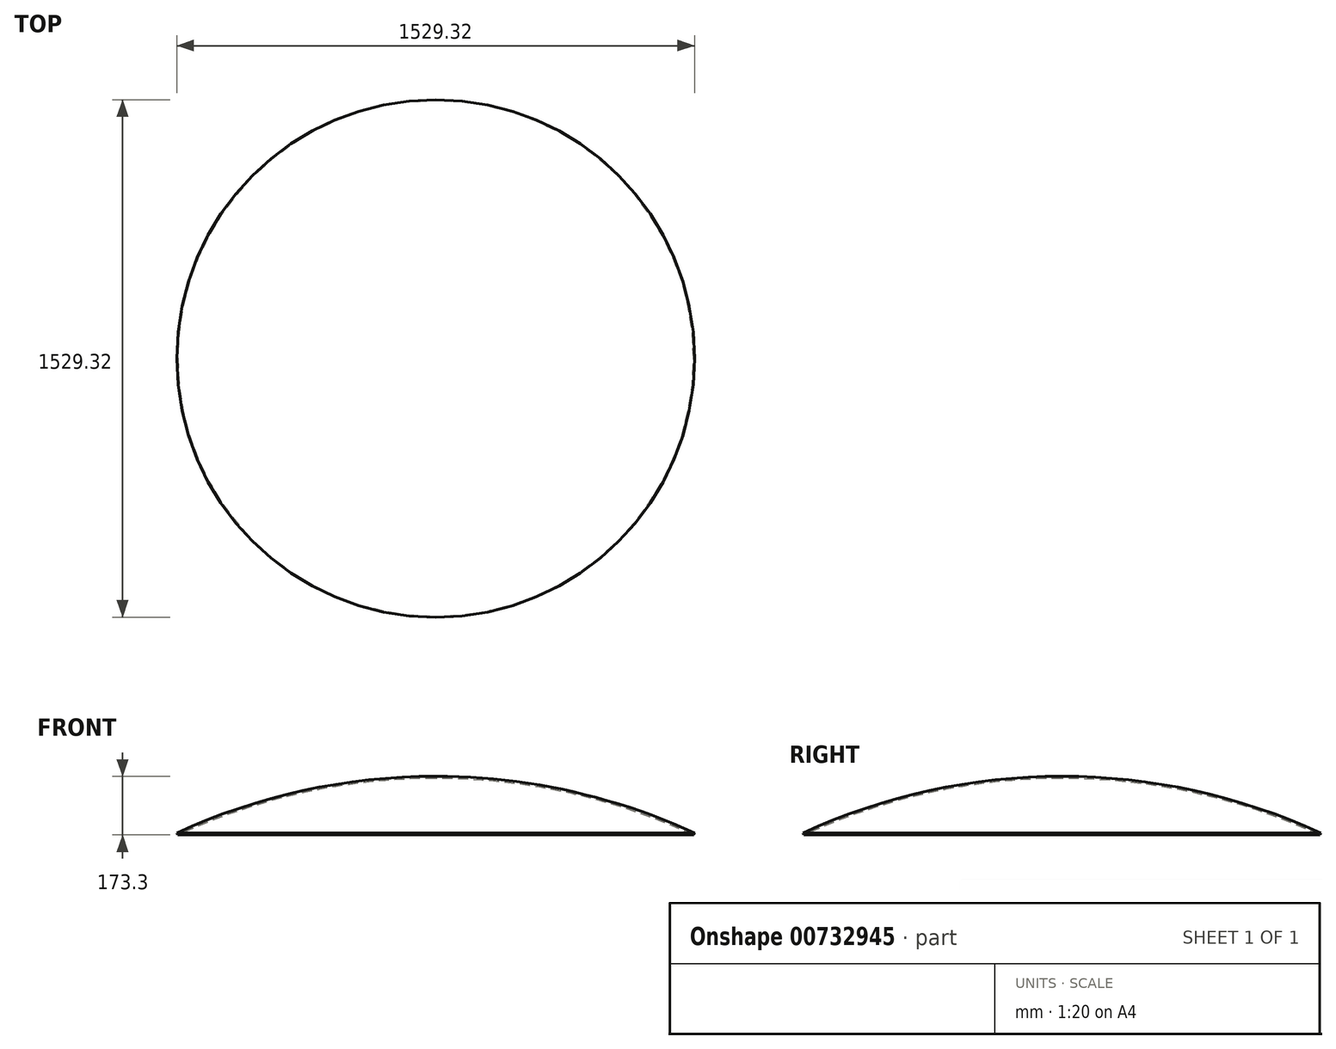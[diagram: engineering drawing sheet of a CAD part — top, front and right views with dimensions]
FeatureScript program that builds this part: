
annotation { "Feature Type Name" : "Feature", "Feature Type Description" : "" }
export const myFeature = defineFeature(function(context is Context, id is Id, definition is map)
    precondition{}
    {
        {
            var Q0;
            Q0=qCreatedBy(makeId("Front.planeOp"),FACE);
            var sketch = newSketch(context, id + "F0", { "sketchPlane" : qUnion([Q0])});
            skArc(sketch, "E0", {"start": v(764.66, 1661.27) * mm, "mid": v(391.4, 1786.43) * mm, "end": v(0, 1828.8) * mm});
            skArc(sketch, "E1", {"start": v(762, 1655.5) * mm, "mid": v(390.04, 1780.22) * mm, "end": v(0, 1822.45) * mm});
            skLineSegment(sketch, "E2", {"start": v(0, 1828.8) * mm, "end": v(0, 1822.45) * mm});
            skLineSegment(sketch, "E3", {"start": v(764.66, 1661.27) * mm, "end": v(762, 1655.5) * mm});
            skSolve(sketch);
        }
        {
            var Q0;
            Q0 = qSketchRegion(id + "F0", true);
            var Q1;
            Q1=sQuery(id+"F0.wireOp",EDGE,"E2");
            revolve(context, id + "F1", {"surfaceOperationType" : NewSurfaceOperationType.NEW, "entities" : qUnion([Q0]), "axis" : qUnion([Q1]), "revolveType" : RevolveType.FULL});
        }
    });
